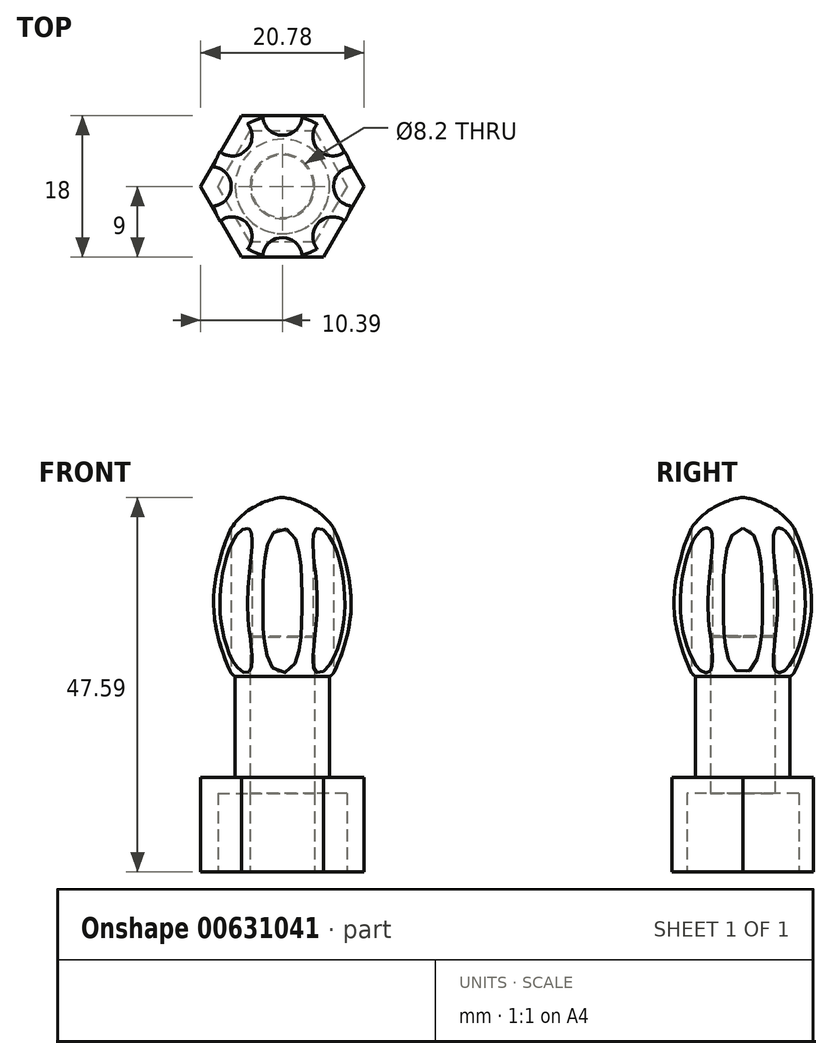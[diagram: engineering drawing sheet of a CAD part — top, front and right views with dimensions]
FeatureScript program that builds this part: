
annotation { "Feature Type Name" : "Feature", "Feature Type Description" : "" }
export const myFeature = defineFeature(function(context is Context, id is Id, definition is map)
    precondition{}
    {
        {
            var Q0;
            Q0=qCreatedBy(makeId("Top.planeOp"),FACE);
            var sketch = newSketch(context, id + "F0", { "sketchPlane" : qUnion([Q0])});
            skCircle(sketch, "E0.cCircle", {"center": v(0, 0) * mm, "radius": 9 * mm, "construction": true});
            skLineSegment(sketch, "E0.0", {"start": v(5.2, -9) * mm, "end": v(-5.2, -9) * mm});
            skLineSegment(sketch, "E0.1", {"start": v(-5.2, -9) * mm, "end": v(-10.4, 0) * mm});
            skLineSegment(sketch, "E0.2", {"start": v(-10.4, 0) * mm, "end": v(-5.2, 9) * mm});
            skLineSegment(sketch, "E0.3", {"start": v(-5.2, 9) * mm, "end": v(5.2, 9) * mm});
            skLineSegment(sketch, "E0.4", {"start": v(5.2, 9) * mm, "end": v(10.4, 0) * mm});
            skLineSegment(sketch, "E0.5", {"start": v(10.4, 0) * mm, "end": v(5.2, -9) * mm});
            skPoint(sketch, "E0.0.midPoint", {"position": v(0, -9) * mm});
            skSolve(sketch);
        }
        {
            var Q0;
            Q0 = qSketchRegion(id + "F0", true);
            extrude(context, id + "F1", {"entities" : qUnion([Q0]), "depth" : 12 * mm, "offsetDistance" : 25 * mm});
        }
        {
            var Q0;
            Q0=qCreatedBy(makeId("Top.planeOp"),FACE);
            var sketch = newSketch(context, id + "F2", { "sketchPlane" : qUnion([Q0])});
            skCircle(sketch, "E1.cCircle", {"center": v(0, 0) * mm, "radius": 7.1 * mm, "construction": true});
            skLineSegment(sketch, "E1.0", {"start": v(4.1, -7.1) * mm, "end": v(-4.1, -7.1) * mm});
            skLineSegment(sketch, "E1.1", {"start": v(-4.1, -7.1) * mm, "end": v(-8.2, 0) * mm});
            skLineSegment(sketch, "E1.2", {"start": v(-8.2, 0) * mm, "end": v(-4.1, 7.1) * mm});
            skLineSegment(sketch, "E1.3", {"start": v(-4.1, 7.1) * mm, "end": v(4.1, 7.1) * mm});
            skLineSegment(sketch, "E1.4", {"start": v(4.1, 7.1) * mm, "end": v(8.2, 0) * mm});
            skLineSegment(sketch, "E1.5", {"start": v(8.2, 0) * mm, "end": v(4.1, -7.1) * mm});
            skPoint(sketch, "E1.0.midPoint", {"position": v(0, -7.1) * mm});
            skSolve(sketch);
        }
        {
            var Q0;
            Q0 = qSketchRegion(id + "F2", true);
            extrude(context, id + "F3", {"entities" : qUnion([Q0]), "operationType" : NewBodyOperationType.REMOVE, "depth" : 10 * mm, "offsetDistance" : 25 * mm});
        }
        {
            var Q0;
            Q0=makeQuery(id+"F1.opExtrude","CAP_FACE",FACE,{"disambiguationData":[OSD([sQuery(id+"F0.wireOp",EDGE,"E0.0"),sQuery(id+"F0.wireOp",EDGE,"E0.1"),sQuery(id+"F0.wireOp",EDGE,"E0.2"),sQuery(id+"F0.wireOp",EDGE,"E0.3"),sQuery(id+"F0.wireOp",EDGE,"E0.4"),sQuery(id+"F0.wireOp",EDGE,"E0.5")])],"isStart":false});
            var sketch = newSketch(context, id + "F4", { "sketchPlane" : qUnion([Q0])});
            skCircle(sketch, "E2", {"center": v(0, 0) * mm, "radius": 6 * mm});
            skSolve(sketch);
        }
        {
            var Q0;
            Q0 = qSketchRegion(id + "F4", true);
            extrude(context, id + "F5", {"entities" : qUnion([Q0]), "operationType" : NewBodyOperationType.ADD, "depth" : 25 * mm, "offsetDistance" : 25 * mm});
        }
        {
            var Q0;
            Q0=makeQuery(id+"F3.boolean.opBoolean","COPY",FACE,{"derivedFrom":makeQuery(id+"F3.opExtrude","CAP_FACE",FACE,{"disambiguationData":[OSD([sQuery(id+"F2.wireOp",EDGE,"E1.0"),sQuery(id+"F2.wireOp",EDGE,"E1.1"),sQuery(id+"F2.wireOp",EDGE,"E1.2"),sQuery(id+"F2.wireOp",EDGE,"E1.3"),sQuery(id+"F2.wireOp",EDGE,"E1.4"),sQuery(id+"F2.wireOp",EDGE,"E1.5")])],"isStart":false})});
            var sketch = newSketch(context, id + "F6", { "sketchPlane" : qUnion([Q0])});
            skCircle(sketch, "E3", {"center": v(0, 0) * mm, "radius": 4.1 * mm});
            skSolve(sketch);
        }
        {
            var Q0;
            Q0 = qSketchRegion(id + "F6", true);
            extrude(context, id + "F7", {"entities" : qUnion([Q0]), "operationType" : NewBodyOperationType.REMOVE, "oppositeDirection" : true, "depth" : 20 * mm, "offsetDistance" : 25 * mm});
        }
        {
            var Q0;
            Q0=qCreatedBy(makeId("Front.planeOp"),FACE);
            var sketch = newSketch(context, id + "F8", { "sketchPlane" : qUnion([Q0])});
            skFitSpline(sketch, "E4", {"points": [v(0, 47.6) * mm, v(-5.28, 45.14) * mm, v(-8.33, 39.38) * mm, v(-8.72, 30.75) * mm, v(-5.86, 24.79) * mm, v(-5.12, 25.92) * mm, v(-4.44, 29.47) * mm, v(0, 30.97) * mm], "startDerivative": vector(-33.86, -4.08) * mm, "endDerivative": vector(30.12, -13.65) * mm});
            skLineSegment(sketch, "E5", {"start": v(0, 0) * mm, "end": v(0, 47.6) * mm, "construction": true});
            skLineSegment(sketch, "E6", {"start": v(0, 47.6) * mm, "end": v(0, 30.97) * mm});
            skSolve(sketch);
        }
        {
            var Q0;
            Q0 = qSketchRegion(id + "F8", true);
            var Q1;
            Q1=sQuery(id+"F8.wireOp",EDGE,"E5");
            revolve(context, id + "F9", {"operationType" : NewBodyOperationType.ADD, "entities" : qUnion([Q0]), "axis" : qUnion([Q1]), "revolveType" : RevolveType.FULL});
        }
        {
            var Q0;
            Q0=makeQuery(id+"F1.opExtrude","CAP_FACE",FACE,{"disambiguationData":[OSD([sQuery(id+"F0.wireOp",EDGE,"E0.0"),sQuery(id+"F0.wireOp",EDGE,"E0.1"),sQuery(id+"F0.wireOp",EDGE,"E0.2"),sQuery(id+"F0.wireOp",EDGE,"E0.3"),sQuery(id+"F0.wireOp",EDGE,"E0.4"),sQuery(id+"F0.wireOp",EDGE,"E0.5")])],"isStart":false});
            var sketch = newSketch(context, id + "F10", { "sketchPlane" : qUnion([Q0])});
            skCircle(sketch, "E7", {"center": v(0, 9) * mm, "radius": 2.5 * mm});
            skPoint(sketch, "E7.centerSnap0", {"position": v(0, 9) * mm});
            skCircle(sketch, "E8.1.0", {"center": v(-6.36, 6.36) * mm, "radius": 2.5 * mm});
            skCircle(sketch, "E8.2.0", {"center": v(-9, 0) * mm, "radius": 2.5 * mm});
            skCircle(sketch, "E8.3.0", {"center": v(-6.36, -6.36) * mm, "radius": 2.5 * mm});
            skCircle(sketch, "E8.4.0", {"center": v(0, -9) * mm, "radius": 2.5 * mm});
            skCircle(sketch, "E8.5.0", {"center": v(6.36, -6.36) * mm, "radius": 2.5 * mm});
            skCircle(sketch, "E8.6.0", {"center": v(9, 0) * mm, "radius": 2.5 * mm});
            skCircle(sketch, "E8.7.0", {"center": v(6.36, 6.36) * mm, "radius": 2.5 * mm});
            skPoint(sketch, "E8.center", {"position": v(0, 0) * mm});
            skSolve(sketch);
        }
        {
            var Q0;
            {var subQ0=sQuery(id+"F10.wireOp",EDGE,"E8.4.0");var subQ1=makeQuery(id+"F1.opExtrude","CAP_EDGE",EDGE,{"disambiguationData":[OSD([sQuery(id+"F0.wireOp",EDGE,"E0.0")])],"isStart":false});var subQ2=makeQuery(id+"F10.imprint","INTERSECT",VERTEX,{"disambiguationData":[OD(0.0)],"derivedFrom":[subQ1,subQ0]});Q0=makeQuery(id+"F10.imprint","IMPRINT",FACE,{"disambiguationData":[TD([[makeQuery(id+"F10.imprint","IMPRINT",EDGE,{"disambiguationData":[TD([[subQ2,1.0]])],"derivedFrom":subQ0}),1.0]])]});}
            var Q1;
            {var subQ0=sQuery(id+"F10.wireOp",EDGE,"E8.4.0");var subQ1=makeQuery(id+"F1.opExtrude","CAP_EDGE",EDGE,{"disambiguationData":[OSD([sQuery(id+"F0.wireOp",EDGE,"E0.0")])],"isStart":false});var subQ2=makeQuery(id+"F10.imprint","INTERSECT",VERTEX,{"disambiguationData":[OD(0.0)],"derivedFrom":[subQ1,subQ0]});Q1=makeQuery(id+"F10.imprint","IMPRINT",FACE,{"disambiguationData":[TD([[makeQuery(id+"F10.imprint","IMPRINT",EDGE,{"disambiguationData":[TD([[subQ2,-1.0]])],"derivedFrom":subQ0}),1.0]])]});}
            var Q2;
            {var subQ0=sQuery(id+"F10.wireOp",EDGE,"E8.5.0");var subQ1=makeQuery(id+"F1.opExtrude","CAP_EDGE",EDGE,{"disambiguationData":[OSD([sQuery(id+"F0.wireOp",EDGE,"E0.5")])],"isStart":false});var subQ2=makeQuery(id+"F10.imprint","INTERSECT",VERTEX,{"disambiguationData":[OD(0.0)],"derivedFrom":[subQ1,subQ0]});Q2=makeQuery(id+"F10.imprint","IMPRINT",FACE,{"disambiguationData":[TD([[makeQuery(id+"F10.imprint","IMPRINT",EDGE,{"disambiguationData":[TD([[subQ2,1.0]])],"derivedFrom":subQ0}),1.0]])]});}
            var Q3;
            {var subQ0=sQuery(id+"F10.wireOp",EDGE,"E8.5.0");var subQ1=makeQuery(id+"F1.opExtrude","CAP_EDGE",EDGE,{"disambiguationData":[OSD([sQuery(id+"F0.wireOp",EDGE,"E0.5")])],"isStart":false});var subQ2=makeQuery(id+"F10.imprint","INTERSECT",VERTEX,{"disambiguationData":[OD(0.0)],"derivedFrom":[subQ1,subQ0]});Q3=makeQuery(id+"F10.imprint","IMPRINT",FACE,{"disambiguationData":[TD([[makeQuery(id+"F10.imprint","IMPRINT",EDGE,{"disambiguationData":[TD([[subQ2,-1.0]])],"derivedFrom":subQ0}),1.0]])]});}
            var Q4;
            {var subQ0=sQuery(id+"F10.wireOp",EDGE,"E8.6.0");var subQ1=makeQuery(id+"F1.opExtrude","CAP_EDGE",EDGE,{"disambiguationData":[OSD([sQuery(id+"F0.wireOp",EDGE,"E0.4")])],"isStart":false});var subQ2=makeQuery(id+"F10.imprint","INTERSECT",VERTEX,{"derivedFrom":[subQ1,subQ0]});Q4=makeQuery(id+"F10.imprint","IMPRINT",FACE,{"disambiguationData":[TD([[makeQuery(id+"F10.imprint","IMPRINT",EDGE,{"disambiguationData":[TD([[subQ2,1.0]])],"derivedFrom":subQ0}),1.0]])]});}
            var Q5;
            {var subQ0=sQuery(id+"F10.wireOp",EDGE,"E8.6.0");var subQ1=makeQuery(id+"F1.opExtrude","CAP_EDGE",EDGE,{"disambiguationData":[OSD([sQuery(id+"F0.wireOp",EDGE,"E0.4")])],"isStart":false});var subQ2=makeQuery(id+"F10.imprint","INTERSECT",VERTEX,{"derivedFrom":[subQ1,subQ0]});Q5=makeQuery(id+"F10.imprint","IMPRINT",FACE,{"disambiguationData":[TD([[makeQuery(id+"F10.imprint","IMPRINT",EDGE,{"disambiguationData":[TD([[subQ2,-1.0]])],"derivedFrom":subQ0}),1.0]])]});}
            var Q6;
            {var subQ0=sQuery(id+"F10.wireOp",EDGE,"E8.3.0");var subQ1=makeQuery(id+"F1.opExtrude","CAP_EDGE",EDGE,{"disambiguationData":[OSD([sQuery(id+"F0.wireOp",EDGE,"E0.1")])],"isStart":false});var subQ2=makeQuery(id+"F10.imprint","INTERSECT",VERTEX,{"disambiguationData":[OD(0.0)],"derivedFrom":[subQ1,subQ0]});Q6=makeQuery(id+"F10.imprint","IMPRINT",FACE,{"disambiguationData":[TD([[makeQuery(id+"F10.imprint","IMPRINT",EDGE,{"disambiguationData":[TD([[subQ2,1.0]])],"derivedFrom":subQ0}),1.0]])]});}
            var Q7;
            {var subQ0=sQuery(id+"F10.wireOp",EDGE,"E8.3.0");var subQ1=makeQuery(id+"F1.opExtrude","CAP_EDGE",EDGE,{"disambiguationData":[OSD([sQuery(id+"F0.wireOp",EDGE,"E0.1")])],"isStart":false});var subQ2=makeQuery(id+"F10.imprint","INTERSECT",VERTEX,{"disambiguationData":[OD(0.0)],"derivedFrom":[subQ1,subQ0]});Q7=makeQuery(id+"F10.imprint","IMPRINT",FACE,{"disambiguationData":[TD([[makeQuery(id+"F10.imprint","IMPRINT",EDGE,{"disambiguationData":[TD([[subQ2,-1.0]])],"derivedFrom":subQ0}),1.0]])]});}
            var Q8;
            {var subQ0=sQuery(id+"F10.wireOp",EDGE,"E8.2.0");var subQ1=makeQuery(id+"F1.opExtrude","CAP_EDGE",EDGE,{"disambiguationData":[OSD([sQuery(id+"F0.wireOp",EDGE,"E0.1")])],"isStart":false});var subQ2=makeQuery(id+"F10.imprint","INTERSECT",VERTEX,{"derivedFrom":[subQ1,subQ0]});Q8=makeQuery(id+"F10.imprint","IMPRINT",FACE,{"disambiguationData":[TD([[makeQuery(id+"F10.imprint","IMPRINT",EDGE,{"disambiguationData":[TD([[subQ2,1.0]])],"derivedFrom":subQ0}),1.0]])]});}
            var Q9;
            {var subQ0=sQuery(id+"F10.wireOp",EDGE,"E8.2.0");var subQ1=makeQuery(id+"F1.opExtrude","CAP_EDGE",EDGE,{"disambiguationData":[OSD([sQuery(id+"F0.wireOp",EDGE,"E0.1")])],"isStart":false});var subQ2=makeQuery(id+"F10.imprint","INTERSECT",VERTEX,{"derivedFrom":[subQ1,subQ0]});Q9=makeQuery(id+"F10.imprint","IMPRINT",FACE,{"disambiguationData":[TD([[makeQuery(id+"F10.imprint","IMPRINT",EDGE,{"disambiguationData":[TD([[subQ2,-1.0]])],"derivedFrom":subQ0}),1.0]])]});}
            var Q10;
            {var subQ0=sQuery(id+"F10.wireOp",EDGE,"E8.1.0");var subQ1=makeQuery(id+"F1.opExtrude","CAP_EDGE",EDGE,{"disambiguationData":[OSD([sQuery(id+"F0.wireOp",EDGE,"E0.2")])],"isStart":false});var subQ2=makeQuery(id+"F10.imprint","INTERSECT",VERTEX,{"disambiguationData":[OD(0.0)],"derivedFrom":[subQ1,subQ0]});Q10=makeQuery(id+"F10.imprint","IMPRINT",FACE,{"disambiguationData":[TD([[makeQuery(id+"F10.imprint","IMPRINT",EDGE,{"disambiguationData":[TD([[subQ2,1.0]])],"derivedFrom":subQ0}),1.0]])]});}
            var Q11;
            {var subQ0=sQuery(id+"F10.wireOp",EDGE,"E8.1.0");var subQ1=makeQuery(id+"F1.opExtrude","CAP_EDGE",EDGE,{"disambiguationData":[OSD([sQuery(id+"F0.wireOp",EDGE,"E0.2")])],"isStart":false});var subQ2=makeQuery(id+"F10.imprint","INTERSECT",VERTEX,{"disambiguationData":[OD(0.0)],"derivedFrom":[subQ1,subQ0]});Q11=makeQuery(id+"F10.imprint","IMPRINT",FACE,{"disambiguationData":[TD([[makeQuery(id+"F10.imprint","IMPRINT",EDGE,{"disambiguationData":[TD([[subQ2,-1.0]])],"derivedFrom":subQ0}),1.0]])]});}
            var Q12;
            {var subQ0=sQuery(id+"F10.wireOp",EDGE,"E7");var subQ1=makeQuery(id+"F1.opExtrude","CAP_EDGE",EDGE,{"disambiguationData":[OSD([sQuery(id+"F0.wireOp",EDGE,"E0.3")])],"isStart":false});var subQ2=makeQuery(id+"F10.imprint","INTERSECT",VERTEX,{"disambiguationData":[OD(0.0)],"derivedFrom":[subQ1,subQ0]});Q12=makeQuery(id+"F10.imprint","IMPRINT",FACE,{"disambiguationData":[TD([[makeQuery(id+"F10.imprint","IMPRINT",EDGE,{"disambiguationData":[TD([[subQ2,1.0]])],"derivedFrom":subQ0}),1.0]])]});}
            var Q13;
            {var subQ0=sQuery(id+"F10.wireOp",EDGE,"E7");var subQ1=makeQuery(id+"F1.opExtrude","CAP_EDGE",EDGE,{"disambiguationData":[OSD([sQuery(id+"F0.wireOp",EDGE,"E0.3")])],"isStart":false});var subQ2=makeQuery(id+"F10.imprint","INTERSECT",VERTEX,{"disambiguationData":[OD(0.0)],"derivedFrom":[subQ1,subQ0]});Q13=makeQuery(id+"F10.imprint","IMPRINT",FACE,{"disambiguationData":[TD([[makeQuery(id+"F10.imprint","IMPRINT",EDGE,{"disambiguationData":[TD([[subQ2,-1.0]])],"derivedFrom":subQ0}),1.0]])]});}
            var Q14;
            {var subQ0=sQuery(id+"F10.wireOp",EDGE,"E8.7.0");var subQ1=makeQuery(id+"F1.opExtrude","CAP_EDGE",EDGE,{"disambiguationData":[OSD([sQuery(id+"F0.wireOp",EDGE,"E0.4")])],"isStart":false});var subQ2=makeQuery(id+"F10.imprint","INTERSECT",VERTEX,{"disambiguationData":[OD(0.0)],"derivedFrom":[subQ1,subQ0]});Q14=makeQuery(id+"F10.imprint","IMPRINT",FACE,{"disambiguationData":[TD([[makeQuery(id+"F10.imprint","IMPRINT",EDGE,{"disambiguationData":[TD([[subQ2,1.0]])],"derivedFrom":subQ0}),1.0]])]});}
            var Q15;
            {var subQ0=sQuery(id+"F10.wireOp",EDGE,"E8.7.0");var subQ1=makeQuery(id+"F1.opExtrude","CAP_EDGE",EDGE,{"disambiguationData":[OSD([sQuery(id+"F0.wireOp",EDGE,"E0.4")])],"isStart":false});var subQ2=makeQuery(id+"F10.imprint","INTERSECT",VERTEX,{"disambiguationData":[OD(0.0)],"derivedFrom":[subQ1,subQ0]});Q15=makeQuery(id+"F10.imprint","IMPRINT",FACE,{"disambiguationData":[TD([[makeQuery(id+"F10.imprint","IMPRINT",EDGE,{"disambiguationData":[TD([[subQ2,-1.0]])],"derivedFrom":subQ0}),1.0]])]});}
            extrude(context, id + "F11", {"entities" : qUnion([Q0, Q1, Q2, Q3, Q4, Q5, Q6, Q7, Q8, Q9, Q10, Q11, Q12, Q13, Q14, Q15]), "operationType" : NewBodyOperationType.REMOVE, "depth" : 35 * mm, "offsetDistance" : 25 * mm});
        }
    });
